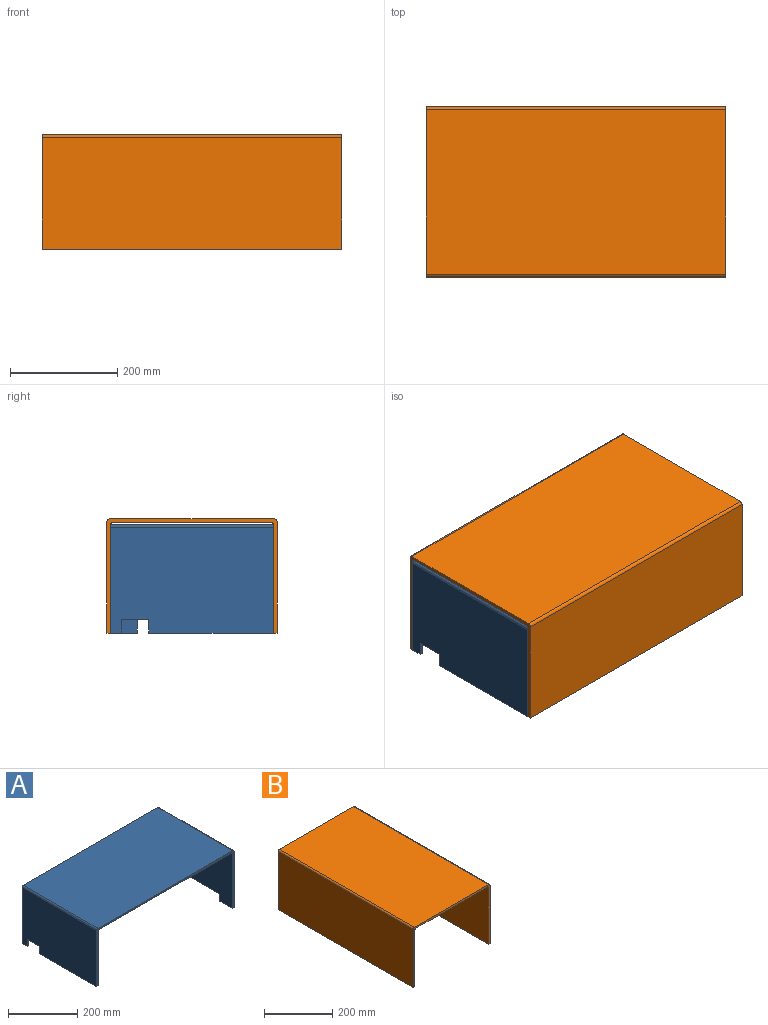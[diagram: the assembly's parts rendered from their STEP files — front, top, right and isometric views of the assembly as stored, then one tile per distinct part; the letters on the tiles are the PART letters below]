
ASSEMBLY  parts=2 mates=1
PART A: 22 faces, bbox 558.8x304.8x203.2 mm
  f0: plane 50.8x6.35mm, normal (0,0,-1), area 322.6mm2, adj f1,f7,f11,f20
  f1: plane 304.8x198.12mm, normal (1,0,0), area 55225.7mm2, adj f0,f8,f10,f11,f14,f19,f20,f21
  f2: plane 233.15x6.35mm, normal (0,0,-1), area 1480.5mm2, adj f3,f4,f10,f17
  f3: plane 304.8x191.77mm, normal (1,0,0), area 57147.9mm2, adj f2,f5,f10,f11,f12,f16,f17,f18
  f4: plane 304.8x198.12mm, normal (-1,0,0), area 59083.4mm2, adj f2,f5,f10,f11,f15,f16,f17,f18
  f5: plane 20.73x6.35mm, normal (0,0,-1), area 131.6mm2, adj f3,f4,f11,f16
  f6: plane 535.94x304.8mm, normal (0,0,-1), area 163354.5mm2, adj f10,f11,f12,f13
  f7: plane 304.8x191.77mm, normal (-1,0,0), area 53290.2mm2, adj f0,f8,f10,f11,f13,f19,f20,f21
  f8: plane 50.8x6.35mm, normal (0,0,-1), area 322.6mm2, adj f1,f7,f10,f19
  f9: plane 548.64x304.8mm, normal (0,0,1), area 167225.5mm2, adj f10,f11,f14,f15
  f10: plane 558.8x203.2mm, normal (0,-1,0), area 6048.4mm2, adj f1,f2,f3,f4,f6,f7,f8,f9
  f11: plane 558.8x203.2mm, normal (0,1,0), area 6048.4mm2, adj f0,f1,f3,f4,f5,f6,f7,f9
  f12: cylinder r=5.08mm len=304.8mm, axis (0,-1,0), area 2432.2mm2, adj f3,f6,f10,f11
  f13: cylinder r=5.08mm len=304.8mm, axis (0,1,0), area 2432.2mm2, adj f6,f7,f10,f11
  f14: cylinder r=5.08mm len=304.8mm, axis (0,1,0), area 2432.2mm2, adj f1,f9,f10,f11
  f15: cylinder r=5.08mm len=304.8mm, axis (0,-1,0), area 2432.2mm2, adj f4,f9,f10,f11
  f16: plane 25.6x6.35mm, normal (0,-1,0), area 162.6mm2, adj f3,f4,f5,f18
  f17: plane 25.6x6.35mm, normal (0,1,0), area 162.6mm2, adj f2,f3,f4,f18
  f18: plane 50.92x6.35mm, normal (0,0,-1), area 323.3mm2, adj f3,f4,f16,f17
  f19: plane 25.4x6.35mm, normal (0,1,0), area 161.3mm2, adj f1,f7,f8,f21
  f20: plane 25.4x6.35mm, normal (0,-1,0), area 161.3mm2, adj f0,f1,f7,f21
  f21: plane 203.2x6.35mm, normal (0,0,-1), area 1290.3mm2, adj f1,f7,f19,f20
PART B: 14 faces, bbox 317.5x558.8x213.4 mm
  f0: plane 558.8x208.28mm, normal (-1,0,0), area 116386.9mm2, adj f1,f8,f9,f13
  f1: plane 558.8x6.35mm, normal (0,0,-1), area 3548.4mm2, adj f0,f2,f8,f9
  f2: plane 558.8x201.93mm, normal (1,0,0), area 112838.5mm2, adj f1,f8,f9,f10
  f3: plane 558.8x294.64mm, normal (0,0,-1), area 164644.8mm2, adj f8,f9,f10,f11
  f4: plane 558.8x201.93mm, normal (-1,0,0), area 112838.5mm2, adj f5,f8,f9,f11
  f5: plane 558.8x6.35mm, normal (0,0,-1), area 3548.4mm2, adj f4,f6,f8,f9
  f6: plane 558.8x208.28mm, normal (1,0,0), area 116386.9mm2, adj f5,f8,f9,f12
  f7: plane 558.8x307.34mm, normal (0,0,1), area 171741.6mm2, adj f8,f9,f12,f13
  f8: plane 317.5x213.36mm, normal (0,-1,0), area 4645.2mm2, adj f0,f1,f2,f3,f4,f5,f6,f7
  f9: plane 317.5x213.36mm, normal (0,1,0), area 4645.2mm2, adj f0,f1,f2,f3,f4,f5,f6,f7
  f10: cylinder r=5.08mm len=558.8mm, axis (0,-1,0), area 4459mm2, adj f2,f3,f8,f9
  f11: cylinder r=5.08mm len=558.8mm, axis (0,1,0), area 4459mm2, adj f3,f4,f8,f9
  f12: cylinder r=5.08mm len=558.8mm, axis (0,1,0), area 4459mm2, adj f6,f7,f8,f9
  f13: cylinder r=5.08mm len=558.8mm, axis (0,-1,0), area 4459mm2, adj f0,f7,f8,f9
PLACE A at identity fixed
PLACE B rot(axis=(0,0,-1),90deg) t=(279.27,-152.78,5.08)mm
MATE planar B.f5 <-> A.f0  axis (0,0,-1) through (-0.13,-308.36,-101.6)mm
